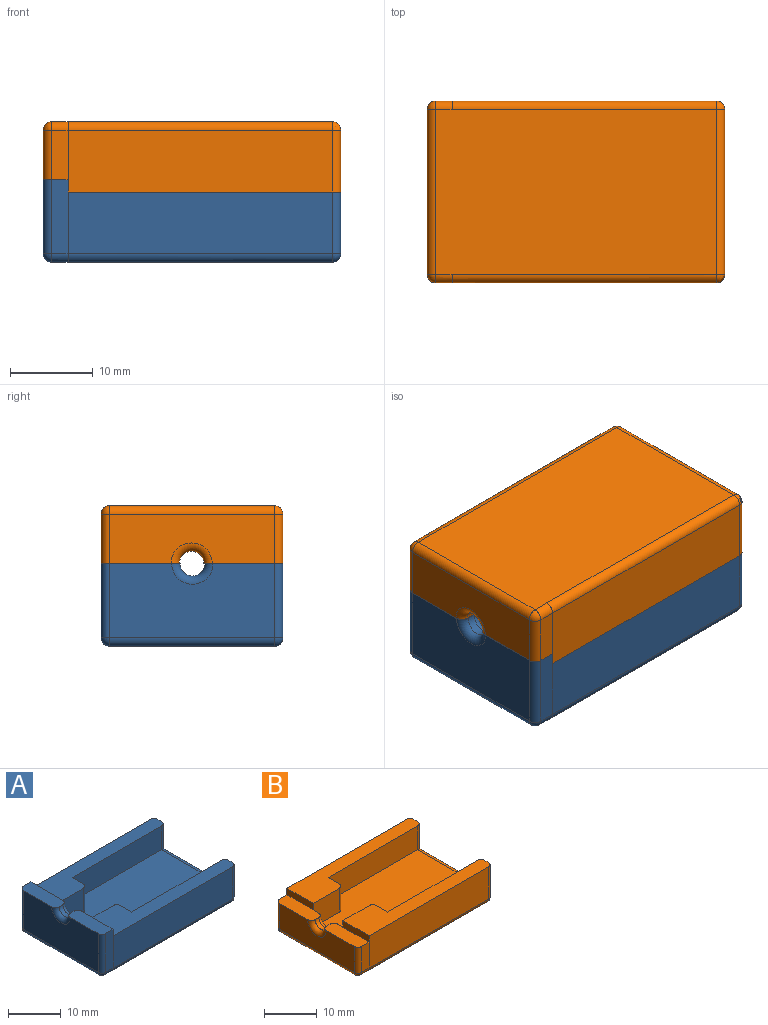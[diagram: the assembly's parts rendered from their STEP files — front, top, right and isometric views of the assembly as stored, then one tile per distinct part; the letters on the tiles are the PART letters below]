
ASSEMBLY  parts=2 mates=1
PART A: 41 faces, bbox 36x22x10 mm
  f0: plane 20x7.5mm, normal (1,0,0), area 33mm2, adj f9,f13,f33,f35,f37,f38,f39,f40
  f1: plane 32x16mm, normal (0,0,1), area 448.4mm2, adj f3,f4,f5,f6,f8,f11,f12,f31
  f2: plane 34x20mm, normal (0,0,-1), area 680mm2, adj f20,f21,f24,f27,f28,f35
  f3: plane 24x5.5mm, normal (0,1,0), area 132mm2, adj f1,f11,f13,f40
  f4: plane 24x5.5mm, normal (0,-1,0), area 132mm2, adj f1,f6,f9,f38
  f5: plane 22x7mm, normal (1,0,0), area 67.2mm2, adj f1,f8,f9,f12,f13,f14,f15,f17
  f6: plane 5.5x3mm, normal (1,0,0), area 16.5mm2, adj f1,f4,f9,f32
  f7: plane 32.02x7.52mm, normal (0,1,0), area 240mm2, adj f9,f14,f20,f33
  f8: plane 7x5.5mm, normal (0,-1,0), area 38.5mm2, adj f1,f5,f9,f32
  f9: plane 33x7mm, normal (0,0,1), area 130.4mm2, adj f0,f4,f5,f6,f7,f8,f32,f33
  f10: plane 32x7.5mm, normal (0,-1,0), area 240mm2, adj f13,f18,f27,f37
  f11: plane 5.5x3mm, normal (1,0,0), area 16.5mm2, adj f1,f3,f13,f31
  f12: plane 7x5.5mm, normal (0,1,0), area 38.5mm2, adj f1,f5,f13,f31
  f13: plane 33x7mm, normal (0,0,1), area 130.4mm2, adj f0,f3,f5,f10,f11,f12,f31,f37
  f14: plane 9.02x2.02mm, normal (0,1,0), area 18mm2, adj f5,f7,f15,f21,f22
  f15: plane 9.54x3mm, normal (0,0,1), area 28mm2, adj f5,f14,f16,f19,f22,f29,f30
  f16: cylinder r=1.5mm len=3mm, axis (1,0,0), area 4.7mm2, adj f15,f17,f29,f30
  f17: plane 9.45x3mm, normal (0,0,1), area 27.7mm2, adj f5,f16,f18,f19,f25,f29,f30
  f18: plane 9x2mm, normal (0,-1,0), area 18mm2, adj f5,f10,f17,f25,f28
  f19: plane 19.99x9mm, normal (-1,0,0), area 170.1mm2, adj f15,f17,f22,f24,f25,f30
  f20: cylinder r=1mm len=32mm, axis (-1,0,0), area 50.3mm2, adj f2,f7,f21,f34
  f21: cylinder r=1mm len=2mm, axis (1,0,0), area 3.1mm2, adj f2,f14,f20,f23
  f22: cylinder r=1mm len=9mm, axis (0,0,-1), area 14.1mm2, adj f14,f15,f19,f23
  f23: sphere r=1mm, area 1.6mm2, adj f21,f22,f24
  f24: cylinder r=1mm len=19.99mm, axis (0,-1,0), area 31.4mm2, adj f2,f19,f23,f26
  f25: cylinder r=1mm len=9mm, axis (0,0,1), area 14.1mm2, adj f17,f18,f19,f26
  f26: sphere r=1mm, area 1.6mm2, adj f24,f25,f28
  f27: cylinder r=1mm len=32mm, axis (1,0,0), area 50.3mm2, adj f2,f10,f28,f36
  f28: cylinder r=1mm len=2mm, axis (1,0,0), area 3.1mm2, adj f2,f18,f26,f27
  f29: torus R=2.5mm, axis (1,0,0), area 9.2mm2, adj f5,f15,f16,f17
  f30: torus R=2.5mm, axis (1,0,0), area 9.2mm2, adj f15,f16,f17,f19
  f31: cylinder r=1mm len=5.5mm, axis (0,0,-1), area 8.6mm2, adj f1,f11,f12,f13
  f32: cylinder r=1mm len=5.5mm, axis (0,0,-1), area 8.6mm2, adj f1,f6,f8,f9
  f33: cylinder r=1mm len=7.5mm, axis (0,0,-1), area 11.8mm2, adj f0,f7,f9,f34
  f34: sphere r=1mm, area 1mm2, adj f20,f33,f35
  f35: cylinder r=1mm len=20mm, axis (0,1,0), area 31.4mm2, adj f0,f2,f34,f36
  f36: sphere r=1mm, area 1.6mm2, adj f27,f35,f37
  f37: cylinder r=1mm len=7.5mm, axis (0,0,-1), area 11.8mm2, adj f0,f10,f13,f36
  f38: cylinder r=1mm len=6.5mm, axis (0,0,1), area 9.4mm2, adj f0,f4,f9,f39
  f39: cylinder r=1mm len=18mm, axis (0,-1,0), area 26.7mm2, adj f0,f1,f38,f40
  f40: cylinder r=1mm len=6.5mm, axis (0,0,-1), area 9.4mm2, adj f0,f3,f13,f39
PART B: 43 faces, bbox 36x22x8.5 mm
  f0: plane 20x7.5mm, normal (1,0,0), area 33mm2, adj f10,f15,f35,f37,f39,f40,f41,f42
  f1: plane 32x16mm, normal (0,0,1), area 448.4mm2, adj f3,f4,f5,f6,f9,f13,f14,f33
  f2: plane 34x20mm, normal (0,0,-1), area 680mm2, adj f22,f23,f26,f29,f30,f37
  f3: plane 8x4mm, normal (1,0,0), area 22.2mm2, adj f1,f9,f14,f16,f18,f31
  f4: plane 24x5.5mm, normal (0,1,0), area 132mm2, adj f1,f13,f15,f42
  f5: plane 24x5.5mm, normal (0,-1,0), area 132mm2, adj f1,f6,f10,f40
  f6: plane 5.5x3mm, normal (1,0,0), area 16.5mm2, adj f1,f5,f10,f34
  f7: plane 32.02x7.52mm, normal (0,1,0), area 240mm2, adj f8,f10,f20,f22,f35
  f8: plane 7x1.5mm, normal (-1,0,0), area 10.5mm2, adj f7,f9,f10,f16
  f9: plane 7x5.5mm, normal (0,-1,0), area 38.5mm2, adj f1,f3,f8,f10,f34
  f10: plane 33x7mm, normal (0,0,1), area 130.4mm2, adj f0,f5,f6,f7,f8,f9,f34,f35
  f11: plane 7x1.5mm, normal (-1,0,0), area 10.5mm2, adj f12,f14,f15,f18
  f12: plane 32x7.5mm, normal (0,-1,0), area 240mm2, adj f11,f15,f19,f29,f39
  f13: plane 5.5x3mm, normal (1,0,0), area 16.5mm2, adj f1,f4,f15,f33
  f14: plane 7x5.5mm, normal (0,1,0), area 38.5mm2, adj f1,f3,f11,f15,f33
  f15: plane 33x7mm, normal (0,0,1), area 130.4mm2, adj f0,f4,f11,f12,f13,f14,f33,f39
  f16: plane 9.55x3mm, normal (0,0,1), area 28mm2, adj f3,f8,f17,f20,f21,f24,f31,f32
  f17: cylinder r=1.5mm len=3mm, axis (1,0,0), area 4.7mm2, adj f16,f18,f31,f32
  f18: plane 9.45x3mm, normal (0,0,1), area 27.7mm2, adj f3,f11,f17,f19,f21,f27,f31,f32
  f19: plane 6x2mm, normal (0,-1,0), area 12mm2, adj f12,f18,f27,f30
  f20: plane 6.02x2.02mm, normal (0,1,0), area 12mm2, adj f7,f16,f23,f24
  f21: plane 19.99x6mm, normal (-1,0,0), area 110.1mm2, adj f16,f18,f24,f26,f27,f32
  f22: cylinder r=1mm len=32mm, axis (-1,0,0), area 50.3mm2, adj f2,f7,f23,f36
  f23: cylinder r=1mm len=2mm, axis (1,0,0), area 3.1mm2, adj f2,f20,f22,f25
  f24: cylinder r=1mm len=6mm, axis (0,0,-1), area 9.4mm2, adj f16,f20,f21,f25
  f25: sphere r=1mm, area 1.6mm2, adj f23,f24,f26
  f26: cylinder r=1mm len=19.99mm, axis (0,-1,0), area 31.4mm2, adj f2,f21,f25,f28
  f27: cylinder r=1mm len=6mm, axis (0,0,1), area 9.4mm2, adj f18,f19,f21,f28
  f28: sphere r=1mm, area 1.6mm2, adj f26,f27,f30
  f29: cylinder r=1mm len=32mm, axis (1,0,0), area 50.3mm2, adj f2,f12,f30,f38
  f30: cylinder r=1mm len=2mm, axis (1,0,0), area 3.1mm2, adj f2,f19,f28,f29
  f31: torus R=2.5mm, axis (1,0,0), area 9.2mm2, adj f3,f16,f17,f18
  f32: torus R=2.5mm, axis (1,0,0), area 9.2mm2, adj f16,f17,f18,f21
  f33: cylinder r=1mm len=5.5mm, axis (0,0,-1), area 8.6mm2, adj f1,f13,f14,f15
  f34: cylinder r=1mm len=5.5mm, axis (0,0,-1), area 8.6mm2, adj f1,f6,f9,f10
  f35: cylinder r=1mm len=7.5mm, axis (0,0,-1), area 11.8mm2, adj f0,f7,f10,f36
  f36: sphere r=1mm, area 1mm2, adj f22,f35,f37
  f37: cylinder r=1mm len=20mm, axis (0,1,0), area 31.4mm2, adj f0,f2,f36,f38
  f38: sphere r=1mm, area 1.6mm2, adj f29,f37,f39
  f39: cylinder r=1mm len=7.5mm, axis (0,0,-1), area 11.8mm2, adj f0,f12,f15,f38
  f40: cylinder r=1mm len=6.5mm, axis (0,0,1), area 9.4mm2, adj f0,f5,f10,f41
  f41: cylinder r=1mm len=18mm, axis (0,-1,0), area 26.7mm2, adj f0,f1,f40,f42
  f42: cylinder r=1mm len=6.5mm, axis (0,0,-1), area 9.4mm2, adj f0,f4,f15,f41
PLACE A t=(-6.45,6.81,-7.24)mm
PLACE B rot(axis=(-1,0,0),180deg) t=(-6.45,-9.19,9.76)mm
MATE fastened B.f16 <-> A.f17  axis (0,0,-1) through (-14.45,-12.19,2.76)mm
